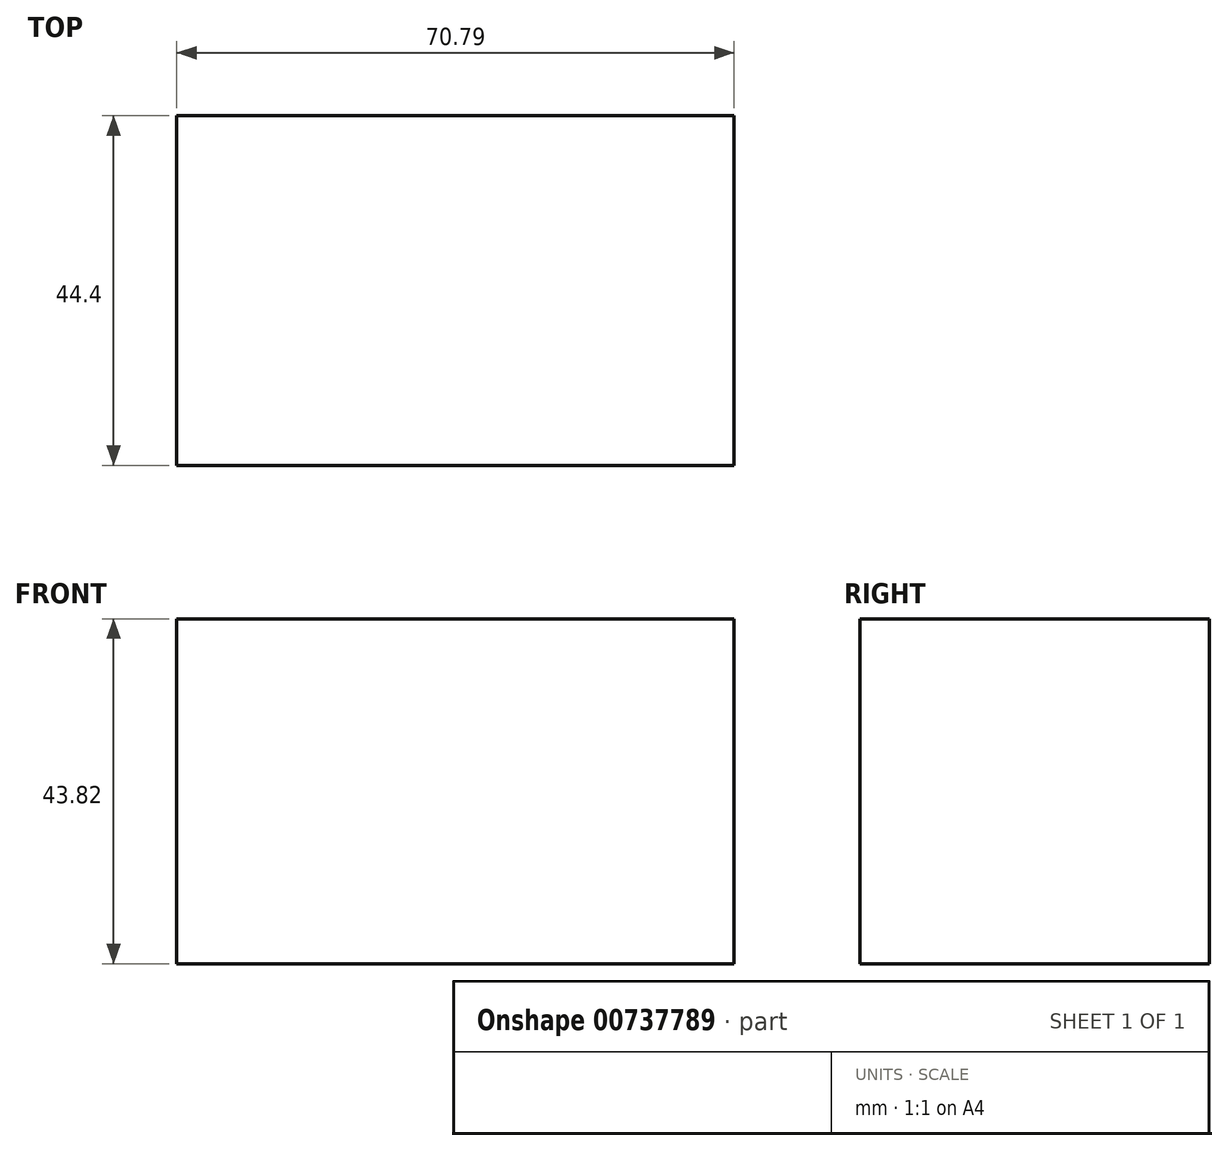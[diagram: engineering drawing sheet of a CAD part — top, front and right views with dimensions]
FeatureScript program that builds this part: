
annotation { "Feature Type Name" : "Feature", "Feature Type Description" : "" }
export const myFeature = defineFeature(function(context is Context, id is Id, definition is map)
    precondition{}
    {
        {
            var Q0;
            Q0=qCreatedBy(makeId("Front.planeOp"),FACE);
            var sketch = newSketch(context, id + "F0", { "sketchPlane" : qUnion([Q0])});
            skLineSegment(sketch, "E0.bottom", {"start": v(-34.47, 21.45) * mm, "end": v(36.32, 21.45) * mm});
            skLineSegment(sketch, "E0.top", {"start": v(-34.47, -22.37) * mm, "end": v(36.32, -22.37) * mm});
            skLineSegment(sketch, "E0.left", {"start": v(-34.47, 21.45) * mm, "end": v(-34.47, -22.37) * mm});
            skLineSegment(sketch, "E0.right", {"start": v(36.32, 21.45) * mm, "end": v(36.32, -22.37) * mm});
            skSolve(sketch);
        }
        {
            var Q0;
            Q0=makeQuery(id+"F0.imprint","IMPRINT",FACE,{"disambiguationData":[TD([[makeQuery(id+"F0.imprint","IMPRINT",EDGE,{"derivedFrom":sQuery(id+"F0.wireOp",EDGE,"E0.bottom")}),-1.0]])]});
            extrude(context, id + "F1", {"entities" : qUnion([Q0]), "depth" : 44.4 * mm, "offsetDistance" : 25 * mm});
        }
    });
